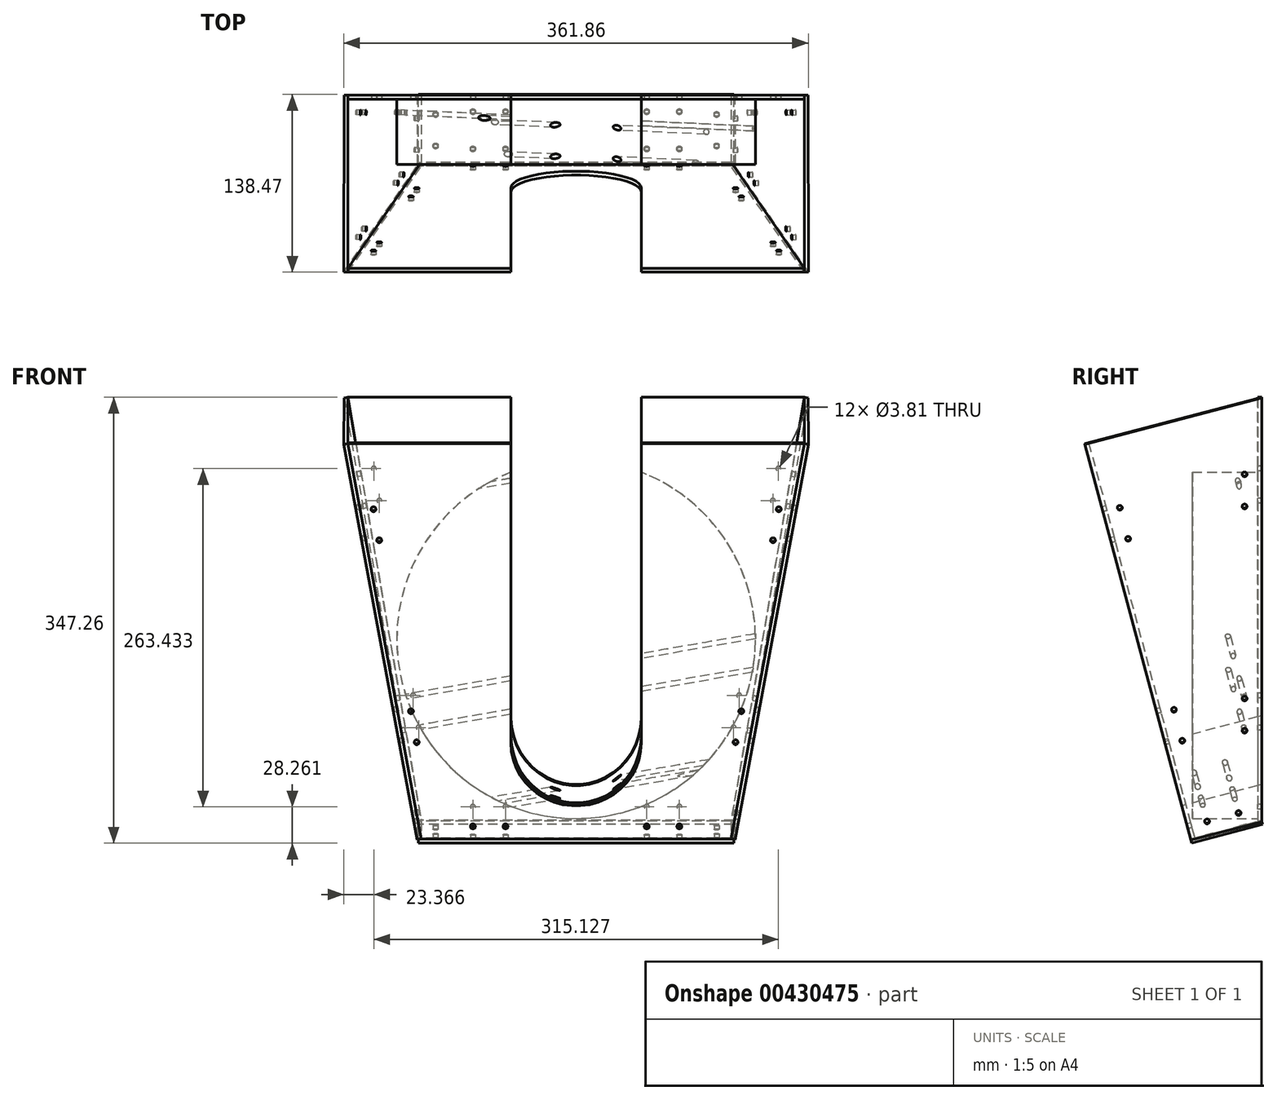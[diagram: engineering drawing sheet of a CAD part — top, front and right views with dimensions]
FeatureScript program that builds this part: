
annotation { "Feature Type Name" : "Feature", "Feature Type Description" : "" }
export const myFeature = defineFeature(function(context is Context, id is Id, definition is map)
    precondition{}
    {
        {
            var Q0;
            Q0=qCreatedBy(makeId("Right.planeOp"),FACE);
            var sketch = newSketch(context, id + "F0", { "sketchPlane" : qUnion([Q0])});
            skLineSegment(sketch, "E0.bottom", {"start": v(-164.52, 79.35) * mm, "end": v(-89.48, 66.12) * mm});
            skLineSegment(sketch, "E0.top", {"start": v(-67.49, 629.66) * mm, "end": v(7.56, 616.43) * mm});
            skLineSegment(sketch, "E0.left", {"start": v(-164.52, 79.35) * mm, "end": v(-67.49, 629.66) * mm});
            skLineSegment(sketch, "E0.right", {"start": v(-89.48, 66.12) * mm, "end": v(7.56, 616.43) * mm});
            skLineSegment(sketch, "E1.bottom", {"start": v(0, 38.1) * mm, "end": v(406.4, 38.1) * mm});
            skLineSegment(sketch, "E1.top", {"start": v(0, 546.1) * mm, "end": v(406.4, 546.1) * mm});
            skLineSegment(sketch, "E1.left", {"start": v(0, 38.1) * mm, "end": v(0, 546.1) * mm});
            skLineSegment(sketch, "E1.right", {"start": v(406.4, 38.1) * mm, "end": v(406.4, 546.1) * mm});
            skLineSegment(sketch, "E2.bottom", {"start": v(42.48, 128.48) * mm, "end": v(86.93, 128.48) * mm});
            skLineSegment(sketch, "E2.top", {"start": v(42.48, 84.03) * mm, "end": v(86.93, 84.03) * mm});
            skLineSegment(sketch, "E2.left", {"start": v(42.48, 128.48) * mm, "end": v(42.48, 84.03) * mm});
            skLineSegment(sketch, "E2.right", {"start": v(86.93, 128.48) * mm, "end": v(86.93, 84.03) * mm});
            skPoint(sketch, "E2.middle", {"position": v(64.7, 106.26) * mm});
            skSolve(sketch);
        }
        {
            var Q0;
            Q0=qCreatedBy(makeId("Front.planeOp"),FACE);
            var sketch = newSketch(context, id + "F1", { "sketchPlane" : qUnion([Q0])});
            skLineSegment(sketch, "E3.bottom", {"start": v(177.8, 596.9) * mm, "end": v(-177.8, 596.9) * mm});
            skLineSegment(sketch, "E3.top", {"start": v(120.65, 266.7) * mm, "end": v(-120.65, 266.7) * mm});
            skPoint(sketch, "E3.middle", {"position": v(0, 431.8) * mm});
            skLineSegment(sketch, "E4", {"start": v(-177.8, 596.9) * mm, "end": v(-120.65, 266.7) * mm});
            skLineSegment(sketch, "E5", {"start": v(0, 596.9) * mm, "end": v(0, 604.14) * mm, "construction": true});
            skPoint(sketch, "E5.endSnap0", {"position": v(0, 596.9) * mm});
            skLineSegment(sketch, "E6.MirrorCS", {"start": v(177.8, 596.9) * mm, "end": v(120.65, 266.7) * mm});
            skCircle(sketch, "E7", {"center": v(0, 408.44) * mm, "radius": 139.7 * mm, "construction": true});
            skCircle(sketch, "E8", {"center": v(0, 330.2) * mm, "radius": 17.46 * mm, "construction": true});
            skPoint(sketch, "E3.left.end.orphan", {"position": v(177.8, 266.7) * mm});
            skPoint(sketch, "E9.orphan", {"position": v(-177.8, 266.7) * mm});
            skSolve(sketch);
        }
        {
            var Q0;
            Q0 = qSketchRegion(id + "F1", true);
            extrude(context, id + "F2", {"entities" : qUnion([Q0]), "oppositeDirection" : true, "depth" : 3.17 * mm});
        }
        {
            var Q0;
            Q0=makeQuery(id+"F1.imprint","IMPRINT",FACE,{"disambiguationData":[TD([[makeQuery(id+"F1.imprint","IMPRINT",EDGE,{"derivedFrom":sQuery(id+"F1.wireOp",EDGE,"E3.bottom")}),1.0]])]});
            var sketch = newSketch(context, id + "F3", { "sketchPlane" : qUnion([Q0])});
            skCircle(sketch, "E10.0", {"center": v(0, 408.44) * mm, "radius": 139.7 * mm});
            skSolve(sketch);
        }
        {
            var Q0;
            Q0 = qSketchRegion(id + "F3", true);
            extrude(context, id + "F4", {"entities" : qUnion([Q0]), "depth" : 50.8 * mm});
        }
        {
            var Q0;
            Q0=makeQuery(id+"F4.opExtrude","CAP_FACE",FACE,{"disambiguationData":[OSD([sQuery(id+"F3.wireOp",EDGE,"E10.0")])],"isStart":false});
            var Q1;
            Q1=sQuery(id+"F1.wireOp",EDGE,"E3.top");
            cPlane(context, id + "F5", {"entities" : qUnion([Q0, Q1]), "cplaneType" : CPlaneType.LINE_ANGLE, "offset" : 25.4 * mm, "angle" : 345 * degree, "width" : 152.4 * mm, "height" : 152.4 * mm});
        }
        {
            var Q0;
            Q0=qCreatedBy(id+"F5.planeOp",FACE);
            cPlane(context, id + "F6", {"entities" : qUnion([Q0]), "cplaneType" : CPlaneType.OFFSET, "offset" : 53.97 * mm, "oppositeDirection" : true, "width" : 152.4 * mm, "height" : 152.4 * mm});
        }
        {
            var Q0;
            Q0=qCreatedBy(id+"F6.planeOp",FACE);
            var sketch = newSketch(context, id + "F7", { "sketchPlane" : qUnion([Q0])});
            skLineSegment(sketch, "E11.0", {"start": v(177.8, 576.56) * mm, "end": v(120.65, 257.61) * mm});
            skLineSegment(sketch, "E11.1", {"start": v(-177.8, 576.56) * mm, "end": v(177.8, 576.56) * mm});
            skLineSegment(sketch, "E11.2", {"start": v(-177.8, 576.56) * mm, "end": v(-120.65, 257.61) * mm});
            skLineSegment(sketch, "E11.3", {"start": v(-120.65, 257.61) * mm, "end": v(120.65, 257.61) * mm});
            skSolve(sketch);
        }
        {
            var Q0;
            Q0=makeQuery(id+"F7.imprint","IMPRINT",FACE,{"disambiguationData":[TD([[makeQuery(id+"F7.imprint","IMPRINT",EDGE,{"derivedFrom":sQuery(id+"F7.wireOp",EDGE,"E11.0")}),-1.0]])]});
            extrude(context, id + "F8", {"entities" : qUnion([Q0]), "depth" : 3.17 * mm});
        }
        {
            var Q0;
            Q0=makeQuery(id+"F8.opExtrude","SWEPT_FACE",FACE,{"disambiguationData":[OSD([sQuery(id+"F7.wireOp",EDGE,"E11.0")])]});
            var sketch = newSketch(context, id + "F9", { "sketchPlane" : qUnion([Q0])});
            skLineSegment(sketch, "E12.0", {"start": v(0.18, 618.48) * mm, "end": v(0.18, 283.37) * mm});
            skLineSegment(sketch, "E13.0", {"start": v(138.18, 582.92) * mm, "end": v(55.54, 269.6) * mm});
            skLineSegment(sketch, "E14", {"start": v(0.18, 283.37) * mm, "end": v(52.47, 270.41) * mm});
            skLineSegment(sketch, "E15", {"start": v(0.18, 618.48) * mm, "end": v(138.18, 582.92) * mm});
            skSolve(sketch);
        }
        {
            var Q0;
            {var subQ0=sQuery(id+"F9.wireOp",EDGE,"E12.0");Q0=makeQuery(id+"F9.imprint","IMPRINT",FACE,{"disambiguationData":[TD([[makeQuery(id+"F9.imprint","IMPRINT",EDGE,{"derivedFrom":subQ0}),1.0]])]});}
            var Q1;
            {var subQ0=sQuery(id+"F9.wireOp",EDGE,"E13.0");Q1=makeQuery(id+"F9.imprint","IMPRINT",FACE,{"disambiguationData":[TD([[makeQuery(id+"F9.imprint","IMPRINT",EDGE,{"derivedFrom":subQ0}),-1.0]])]});}
            extrude(context, id + "F10", {"entities" : qUnion([Q0, Q1]), "depth" : 3.17 * mm});
        }
        {
            var Q0;
            Q0=makeQuery(id+"F10.opExtrude","SWEPT_BODY",BODY,{"disambiguationData":[OSD([sQuery(id+"F7.wireOp",EDGE,"E11.0"),sQuery(id+"F9.wireOp",EDGE,"E12.0"),sQuery(id+"F9.wireOp",EDGE,"E14"),sQuery(id+"F9.wireOp",EDGE,"E15")])]});
            var Q1;
            Q1=qCreatedBy(makeId("Right.planeOp"),FACE);
            mirror(context, id + "F11", {"entities" : qUnion([Q0]), "mirrorPlane" : qUnion([Q1])});
        }
        {
            var Q0;
            Q0=makeQuery(id+"F8.opExtrude","SWEPT_FACE",FACE,{"disambiguationData":[OSD([sQuery(id+"F7.wireOp",EDGE,"E11.3")])]});
            var sketch = newSketch(context, id + "F12", { "sketchPlane" : qUnion([Q0])});
            skLineSegment(sketch, "E16.bottom", {"start": v(122.9, -15.05) * mm, "end": v(-122.9, -15.05) * mm});
            skLineSegment(sketch, "E16.top", {"start": v(122.9, -72.1) * mm, "end": v(-122.9, -72.1) * mm});
            skLineSegment(sketch, "E16.left", {"start": v(122.9, -15.05) * mm, "end": v(122.9, -72.1) * mm});
            skLineSegment(sketch, "E16.right", {"start": v(-122.9, -15.05) * mm, "end": v(-122.9, -72.1) * mm});
            skPoint(sketch, "E16.middle", {"position": v(0, -43.57) * mm});
            skSolve(sketch);
        }
        {
            var Q0;
            Q0 = qSketchRegion(id + "F12", true);
            extrude(context, id + "F13", {"entities" : qUnion([Q0]), "depth" : 3.17 * mm});
        }
        {
            var Q0;
            Q0=makeQuery(id+"F8.opExtrude","CAP_FACE",FACE,{"disambiguationData":[OSD([sQuery(id+"F7.wireOp",EDGE,"E11.0"),sQuery(id+"F7.wireOp",EDGE,"E11.1"),sQuery(id+"F7.wireOp",EDGE,"E11.2"),sQuery(id+"F7.wireOp",EDGE,"E11.3")])],"isStart":true});
            var sketch = newSketch(context, id + "F14", { "sketchPlane" : qUnion([Q0])});
            skLineSegment(sketch, "E17", {"start": v(0, 439.09) * mm, "end": v(0, 333.36) * mm, "construction": true});
            skLineSegment(sketch, "E18.bottom", {"start": v(-170.23, 534.32) * mm, "end": v(-149.92, 537.96) * mm, "construction": true});
            skLineSegment(sketch, "E18.top", {"start": v(-161.27, 484.32) * mm, "end": v(-140.96, 487.96) * mm, "construction": true});
            skLineSegment(sketch, "E18.left", {"start": v(-170.23, 534.32) * mm, "end": v(-161.27, 484.32) * mm, "construction": true});
            skLineSegment(sketch, "E18.right", {"start": v(-149.92, 537.96) * mm, "end": v(-140.96, 487.96) * mm, "construction": true});
            skLineSegment(sketch, "E19.bottom", {"start": v(-93.12, 278.25) * mm, "end": v(-42.32, 278.25) * mm, "construction": true});
            skLineSegment(sketch, "E19.top", {"start": v(-93.12, 257.61) * mm, "end": v(-42.32, 257.61) * mm});
            skLineSegment(sketch, "E19.left", {"start": v(-93.12, 278.25) * mm, "end": v(-93.12, 257.61) * mm, "construction": true});
            skLineSegment(sketch, "E19.right", {"start": v(-42.32, 278.25) * mm, "end": v(-42.32, 257.61) * mm, "construction": true});
            skLineSegment(sketch, "E20", {"start": v(-160.07, 536.14) * mm, "end": v(-151.11, 486.14) * mm, "construction": true});
            skLineSegment(sketch, "E21", {"start": v(-93.12, 267.93) * mm, "end": v(-42.32, 267.93) * mm, "construction": true});
            skLineSegment(sketch, "E22", {"start": v(-145.44, 512.96) * mm, "end": v(-165.75, 509.32) * mm, "construction": true});
            skLineSegment(sketch, "E23", {"start": v(-67.72, 278.25) * mm, "end": v(-67.72, 257.61) * mm, "construction": true});
            skCircle(sketch, "E24", {"center": v(-157.83, 523.64) * mm, "radius": 1.9 * mm});
            skCircle(sketch, "E25.MirrorC", {"center": v(-153.35, 498.64) * mm, "radius": 1.9 * mm});
            skLineSegment(sketch, "E26.bottom", {"start": v(-141.04, 371.42) * mm, "end": v(-120.73, 375.06) * mm, "construction": true});
            skLineSegment(sketch, "E26.top", {"start": v(-132.08, 321.41) * mm, "end": v(-111.77, 325.05) * mm, "construction": true});
            skLineSegment(sketch, "E26.left", {"start": v(-141.04, 371.42) * mm, "end": v(-132.08, 321.41) * mm, "construction": true});
            skLineSegment(sketch, "E26.right", {"start": v(-120.73, 375.06) * mm, "end": v(-111.77, 325.05) * mm, "construction": true});
            skLineSegment(sketch, "E27", {"start": v(-130.88, 373.24) * mm, "end": v(-121.92, 323.23) * mm, "construction": true});
            skLineSegment(sketch, "E28", {"start": v(-116.25, 350.05) * mm, "end": v(-136.56, 346.41) * mm, "construction": true});
            skCircle(sketch, "E29", {"center": v(-128.64, 360.73) * mm, "radius": 1.9 * mm});
            skCircle(sketch, "E30.MirrorC", {"center": v(-124.16, 335.73) * mm, "radius": 1.9 * mm});
            skCircle(sketch, "E31", {"center": v(-80.42, 267.93) * mm, "radius": 1.9 * mm});
            skCircle(sketch, "E32.MirrorC", {"center": v(-55.02, 267.93) * mm, "radius": 1.9 * mm});
            skLineSegment(sketch, "E33.MirrorCS", {"start": v(132.08, 321.41) * mm, "end": v(111.77, 325.05) * mm, "construction": true});
            skCircle(sketch, "E34.MirrorC", {"center": v(128.64, 360.73) * mm, "radius": 1.9 * mm});
            skCircle(sketch, "E35.MirrorC", {"center": v(157.83, 523.64) * mm, "radius": 1.9 * mm});
            skLineSegment(sketch, "E36.MirrorCS", {"start": v(42.32, 278.25) * mm, "end": v(42.32, 257.61) * mm, "construction": true});
            skLineSegment(sketch, "E37.MirrorCS", {"start": v(93.12, 278.25) * mm, "end": v(93.12, 257.61) * mm, "construction": true});
            skLineSegment(sketch, "E38.MirrorCS", {"start": v(161.27, 484.32) * mm, "end": v(140.96, 487.96) * mm, "construction": true});
            skCircle(sketch, "E39.MirrorC", {"center": v(55.02, 267.93) * mm, "radius": 1.9 * mm});
            skLineSegment(sketch, "E40.MirrorCS", {"start": v(145.44, 512.96) * mm, "end": v(165.75, 509.32) * mm, "construction": true});
            skLineSegment(sketch, "E41.MirrorCS", {"start": v(170.23, 534.32) * mm, "end": v(149.92, 537.96) * mm, "construction": true});
            skLineSegment(sketch, "E42.MirrorCS", {"start": v(130.88, 373.24) * mm, "end": v(121.92, 323.23) * mm, "construction": true});
            skCircle(sketch, "E43.MirrorC", {"center": v(124.16, 335.73) * mm, "radius": 1.9 * mm});
            skLineSegment(sketch, "E44.MirrorCS", {"start": v(160.07, 536.14) * mm, "end": v(151.11, 486.14) * mm, "construction": true});
            skLineSegment(sketch, "E45.MirrorCS", {"start": v(141.04, 371.42) * mm, "end": v(120.73, 375.06) * mm, "construction": true});
            skCircle(sketch, "E46.MirrorC", {"center": v(153.35, 498.64) * mm, "radius": 1.9 * mm});
            skCircle(sketch, "E47.MirrorC", {"center": v(80.42, 267.93) * mm, "radius": 1.9 * mm});
            skLineSegment(sketch, "E48.MirrorCS", {"start": v(141.04, 371.42) * mm, "end": v(132.08, 321.41) * mm, "construction": true});
            skLineSegment(sketch, "E49.MirrorCS", {"start": v(93.12, 257.61) * mm, "end": v(42.32, 257.61) * mm});
            skLineSegment(sketch, "E50.MirrorCS", {"start": v(116.25, 350.05) * mm, "end": v(136.56, 346.41) * mm, "construction": true});
            skLineSegment(sketch, "E51.MirrorCS", {"start": v(170.23, 534.32) * mm, "end": v(161.27, 484.32) * mm, "construction": true});
            skLineSegment(sketch, "E52.MirrorCS", {"start": v(149.92, 537.96) * mm, "end": v(140.96, 487.96) * mm, "construction": true});
            skLineSegment(sketch, "E53.MirrorCS", {"start": v(120.73, 375.06) * mm, "end": v(111.77, 325.05) * mm, "construction": true});
            skLineSegment(sketch, "E54.MirrorCS", {"start": v(93.12, 267.93) * mm, "end": v(42.32, 267.93) * mm, "construction": true});
            skLineSegment(sketch, "E55.MirrorCS", {"start": v(67.72, 278.25) * mm, "end": v(67.72, 257.61) * mm, "construction": true});
            skLineSegment(sketch, "E56.MirrorCS", {"start": v(93.12, 278.25) * mm, "end": v(42.32, 278.25) * mm, "construction": true});
            skSolve(sketch);
        }
        {
            var Q0;
            Q0 = qSketchRegion(id + "F14", true);
            var Q1;
            Q1=makeQuery(id+"F8.opExtrude","CAP_FACE",FACE,{"disambiguationData":[OSD([sQuery(id+"F7.wireOp",EDGE,"E11.0"),sQuery(id+"F7.wireOp",EDGE,"E11.1"),sQuery(id+"F7.wireOp",EDGE,"E11.2"),sQuery(id+"F7.wireOp",EDGE,"E11.3")])],"isStart":false});
            extrude(context, id + "F15", {"entities" : qUnion([Q0]), "operationType" : NewBodyOperationType.REMOVE, "endBound" : BoundingType.UP_TO_SURFACE, "oppositeDirection" : true, "depth" : 25.4 * mm, "endBoundEntityFace" : qUnion([Q1]), "offsetDistance" : 25.4 * mm});
        }
        {
            var Q0;
            Q0=makeQuery(id+"F10.opExtrude","CAP_FACE",FACE,{"disambiguationData":[OSD([sQuery(id+"F7.wireOp",EDGE,"E11.0"),sQuery(id+"F7.wireOp",EDGE,"E11.3"),sQuery(id+"F9.wireOp",EDGE,"E12.0"),sQuery(id+"F9.wireOp",EDGE,"E13.0"),sQuery(id+"F9.wireOp",EDGE,"E14"),sQuery(id+"F9.wireOp",EDGE,"E15")])],"isStart":false});
            var sketch = newSketch(context, id + "F16", { "sketchPlane" : qUnion([Q0])});
            skLineSegment(sketch, "E57.0", {"start": v(127.23, 541.42) * mm, "end": v(114.28, 492.3) * mm, "construction": true});
            skLineSegment(sketch, "E58.0", {"start": v(85.03, 381.4) * mm, "end": v(72.07, 332.28) * mm, "construction": true});
            skLineSegment(sketch, "E59.bottom", {"start": v(62, 387.47) * mm, "end": v(85.03, 381.4) * mm, "construction": true});
            skLineSegment(sketch, "E59.top", {"start": v(49.05, 338.35) * mm, "end": v(72.07, 332.28) * mm, "construction": true});
            skLineSegment(sketch, "E59.left", {"start": v(62, 387.47) * mm, "end": v(49.05, 338.35) * mm, "construction": true});
            skLineSegment(sketch, "E60", {"start": v(81.96, 382.2) * mm, "end": v(69, 333.09) * mm, "construction": true});
            skPoint(sketch, "E61", {"position": v(71.98, 384.84) * mm});
            skLineSegment(sketch, "E62", {"start": v(71.98, 384.84) * mm, "end": v(59.02, 335.72) * mm, "construction": true});
            skLineSegment(sketch, "E63", {"start": v(55.52, 362.9) * mm, "end": v(75.48, 357.65) * mm, "construction": true});
            skCircle(sketch, "E64", {"center": v(62.26, 348) * mm, "radius": 1.9 * mm});
            skCircle(sketch, "E65.MirrorC", {"center": v(68.74, 372.56) * mm, "radius": 1.9 * mm});
            skLineSegment(sketch, "E66.bottom", {"start": v(104.2, 547.5) * mm, "end": v(127.23, 541.42) * mm, "construction": true});
            skLineSegment(sketch, "E66.top", {"start": v(91.25, 498.37) * mm, "end": v(114.28, 492.3) * mm, "construction": true});
            skLineSegment(sketch, "E66.left", {"start": v(104.2, 547.5) * mm, "end": v(91.25, 498.37) * mm, "construction": true});
            skLineSegment(sketch, "E67", {"start": v(124.16, 542.23) * mm, "end": v(111.2, 493.11) * mm, "construction": true});
            skPoint(sketch, "E68", {"position": v(114.18, 544.86) * mm});
            skLineSegment(sketch, "E69", {"start": v(114.18, 544.86) * mm, "end": v(101.23, 495.74) * mm, "construction": true});
            skLineSegment(sketch, "E70", {"start": v(97.73, 522.93) * mm, "end": v(117.68, 517.67) * mm, "construction": true});
            skCircle(sketch, "E71", {"center": v(104.47, 508.02) * mm, "radius": 1.9 * mm});
            skCircle(sketch, "E72.MirrorC", {"center": v(110.95, 532.58) * mm, "radius": 1.9 * mm});
            skLineSegment(sketch, "E73.bottom", {"start": v(3.35, 570.93) * mm, "end": v(24, 570.93) * mm, "construction": true});
            skLineSegment(sketch, "E73.top", {"start": v(3.35, 520.13) * mm, "end": v(24, 520.13) * mm, "construction": true});
            skLineSegment(sketch, "E73.left", {"start": v(3.35, 570.93) * mm, "end": v(3.35, 520.13) * mm, "construction": true});
            skLineSegment(sketch, "E73.right", {"start": v(24, 570.93) * mm, "end": v(24, 520.13) * mm, "construction": true});
            skLineSegment(sketch, "E74.bottom", {"start": v(3.35, 570.93) * mm, "end": v(0.18, 570.93) * mm, "construction": true});
            skLineSegment(sketch, "E74.top", {"start": v(3.35, 520.13) * mm, "end": v(0.18, 520.13) * mm, "construction": true});
            skLineSegment(sketch, "E74.right", {"start": v(0.18, 570.93) * mm, "end": v(0.18, 520.13) * mm, "construction": true});
            skLineSegment(sketch, "E75", {"start": v(13.67, 570.93) * mm, "end": v(13.67, 520.13) * mm, "construction": true});
            skLineSegment(sketch, "E76", {"start": v(24, 545.53) * mm, "end": v(3.35, 545.53) * mm, "construction": true});
            skCircle(sketch, "E77", {"center": v(13.67, 558.23) * mm, "radius": 1.9 * mm});
            skCircle(sketch, "E78.MirrorC", {"center": v(13.67, 532.83) * mm, "radius": 1.9 * mm});
            skLineSegment(sketch, "E79.bottom", {"start": v(3.35, 393.68) * mm, "end": v(24, 393.68) * mm, "construction": true});
            skLineSegment(sketch, "E79.top", {"start": v(3.35, 342.88) * mm, "end": v(24, 342.88) * mm, "construction": true});
            skLineSegment(sketch, "E79.left", {"start": v(3.35, 393.68) * mm, "end": v(3.35, 342.88) * mm, "construction": true});
            skLineSegment(sketch, "E79.right", {"start": v(24, 393.68) * mm, "end": v(24, 342.88) * mm, "construction": true});
            skLineSegment(sketch, "E80.bottom", {"start": v(3.35, 393.68) * mm, "end": v(0.18, 393.68) * mm, "construction": true});
            skLineSegment(sketch, "E80.top", {"start": v(3.35, 342.88) * mm, "end": v(0.18, 342.88) * mm, "construction": true});
            skLineSegment(sketch, "E80.right", {"start": v(0.18, 393.68) * mm, "end": v(0.18, 342.88) * mm, "construction": true});
            skLineSegment(sketch, "E81", {"start": v(13.67, 393.68) * mm, "end": v(13.67, 342.88) * mm, "construction": true});
            skLineSegment(sketch, "E82", {"start": v(24, 368.28) * mm, "end": v(3.35, 368.28) * mm, "construction": true});
            skCircle(sketch, "E83", {"center": v(13.67, 380.98) * mm, "radius": 1.9 * mm});
            skCircle(sketch, "E84.MirrorC", {"center": v(13.67, 355.58) * mm, "radius": 1.9 * mm});
            skLineSegment(sketch, "E85.bottom", {"start": v(8.73, 303.76) * mm, "end": v(57.85, 290.8) * mm, "construction": true});
            skLineSegment(sketch, "E85.top", {"start": v(3.46, 283.8) * mm, "end": v(52.58, 270.85) * mm, "construction": true});
            skLineSegment(sketch, "E85.left", {"start": v(8.73, 303.76) * mm, "end": v(3.46, 283.8) * mm, "construction": true});
            skLineSegment(sketch, "E85.right", {"start": v(57.85, 290.8) * mm, "end": v(52.58, 270.85) * mm, "construction": true});
            skLineSegment(sketch, "E86.top", {"start": v(2.65, 280.73) * mm, "end": v(51.77, 267.78) * mm, "construction": true});
            skLineSegment(sketch, "E86.left", {"start": v(3.46, 283.8) * mm, "end": v(2.65, 280.73) * mm, "construction": true});
            skLineSegment(sketch, "E86.right", {"start": v(52.58, 270.85) * mm, "end": v(51.77, 267.78) * mm, "construction": true});
            skLineSegment(sketch, "E87", {"start": v(6.1, 293.78) * mm, "end": v(55.22, 280.82) * mm, "construction": true});
            skLineSegment(sketch, "E88", {"start": v(33.29, 297.28) * mm, "end": v(28.02, 277.32) * mm, "construction": true});
            skCircle(sketch, "E89", {"center": v(18.38, 290.54) * mm, "radius": 1.9 * mm});
            skCircle(sketch, "E90.MirrorC", {"center": v(42.94, 284.06) * mm, "radius": 1.9 * mm});
            skSolve(sketch);
        }
        {
            var Q0;
            Q0 = qSketchRegion(id + "F16", true);
            extrude(context, id + "F17", {"entities" : qUnion([Q0]), "operationType" : NewBodyOperationType.REMOVE, "endBound" : BoundingType.THROUGH_ALL, "oppositeDirection" : true, "depth" : 25.4 * mm, "offsetDistance" : 25.4 * mm});
        }
        {
            var Q0;
            Q0=makeQuery(id+"F11.opPattern","COPY",BODY,{"derivedFrom":makeQuery(id+"F10.opExtrude","SWEPT_BODY",BODY,{"disambiguationData":[OSD([sQuery(id+"F7.wireOp",EDGE,"E11.0"),sQuery(id+"F7.wireOp",EDGE,"E11.3"),sQuery(id+"F9.wireOp",EDGE,"E12.0"),sQuery(id+"F9.wireOp",EDGE,"E13.0"),sQuery(id+"F9.wireOp",EDGE,"E14"),sQuery(id+"F9.wireOp",EDGE,"E15")])]}),"instanceName":"1"});
            deleteBodies(context, id + "F18", {"entities" : qUnion([Q0])});
        }
        {
            var Q0;
            Q0=makeQuery(id+"F10.opExtrude","SWEPT_BODY",BODY,{"disambiguationData":[OSD([sQuery(id+"F7.wireOp",EDGE,"E11.0"),sQuery(id+"F7.wireOp",EDGE,"E11.3"),sQuery(id+"F9.wireOp",EDGE,"E12.0"),sQuery(id+"F9.wireOp",EDGE,"E13.0"),sQuery(id+"F9.wireOp",EDGE,"E14"),sQuery(id+"F9.wireOp",EDGE,"E15")])]});
            var Q1;
            Q1=qCreatedBy(makeId("Right.planeOp"),FACE);
            mirror(context, id + "F19", {"entities" : qUnion([Q0]), "mirrorPlane" : qUnion([Q1])});
        }
        {
            var Q0;
            Q0=makeQuery(id+"F1.imprint","IMPRINT",FACE,{"disambiguationData":[TD([[makeQuery(id+"F1.imprint","IMPRINT",EDGE,{"derivedFrom":sQuery(id+"F1.wireOp",EDGE,"E3.bottom")}),1.0]])]});
            var sketch = newSketch(context, id + "F20", { "sketchPlane" : qUnion([Q0])});
            skLineSegment(sketch, "E91.0", {"start": v(-172.82, 549.5) * mm, "end": v(-164.15, 499.45) * mm, "construction": true});
            skLineSegment(sketch, "E92.bottom", {"start": v(-169.9, 552.1) * mm, "end": v(-173.03, 551.57) * mm, "construction": true});
            skLineSegment(sketch, "E92.top", {"start": v(-161.23, 502.05) * mm, "end": v(-164.36, 501.51) * mm, "construction": true});
            skLineSegment(sketch, "E92.left", {"start": v(-169.9, 552.1) * mm, "end": v(-161.23, 502.05) * mm, "construction": true});
            skLineSegment(sketch, "E92.right", {"start": v(-173.03, 551.57) * mm, "end": v(-164.36, 501.51) * mm, "construction": true});
            skLineSegment(sketch, "E93.bottom", {"start": v(-149.56, 555.63) * mm, "end": v(-169.9, 552.1) * mm, "construction": true});
            skLineSegment(sketch, "E93.top", {"start": v(-140.9, 505.57) * mm, "end": v(-161.23, 502.05) * mm, "construction": true});
            skLineSegment(sketch, "E93.left", {"start": v(-149.56, 555.63) * mm, "end": v(-140.9, 505.57) * mm, "construction": true});
            skLineSegment(sketch, "E94", {"start": v(-159.73, 553.87) * mm, "end": v(-151.07, 503.81) * mm, "construction": true});
            skLineSegment(sketch, "E95", {"start": v(-145.23, 530.6) * mm, "end": v(-165.57, 527.08) * mm, "construction": true});
            skCircle(sketch, "E96", {"center": v(-157.56, 541.35) * mm, "radius": 1.9 * mm});
            skCircle(sketch, "E97.MirrorC", {"center": v(-153.23, 516.33) * mm, "radius": 1.9 * mm});
            skLineSegment(sketch, "E98", {"start": v(0, 542.09) * mm, "end": v(0, 433.89) * mm, "construction": true});
            skLineSegment(sketch, "E99.0", {"start": v(-137.98, 349.1) * mm, "end": v(-129.32, 299.04) * mm, "construction": true});
            skLineSegment(sketch, "E100.bottom", {"start": v(-139.32, 375.42) * mm, "end": v(-142.45, 374.88) * mm, "construction": true});
            skLineSegment(sketch, "E100.top", {"start": v(-130.65, 325.37) * mm, "end": v(-133.78, 324.83) * mm, "construction": true});
            skLineSegment(sketch, "E100.left", {"start": v(-139.32, 375.42) * mm, "end": v(-130.65, 325.37) * mm, "construction": true});
            skLineSegment(sketch, "E100.right", {"start": v(-142.45, 374.88) * mm, "end": v(-133.78, 324.83) * mm, "construction": true});
            skLineSegment(sketch, "E101.bottom", {"start": v(-118.98, 378.94) * mm, "end": v(-139.32, 375.42) * mm, "construction": true});
            skLineSegment(sketch, "E101.top", {"start": v(-110.32, 328.89) * mm, "end": v(-130.65, 325.37) * mm, "construction": true});
            skLineSegment(sketch, "E101.left", {"start": v(-118.98, 378.94) * mm, "end": v(-110.32, 328.89) * mm, "construction": true});
            skLineSegment(sketch, "E102", {"start": v(-129.15, 377.18) * mm, "end": v(-120.49, 327.13) * mm, "construction": true});
            skLineSegment(sketch, "E103", {"start": v(-114.65, 353.92) * mm, "end": v(-134.99, 350.4) * mm, "construction": true});
            skCircle(sketch, "E104", {"center": v(-126.98, 364.67) * mm, "radius": 1.9 * mm});
            skCircle(sketch, "E105.MirrorC", {"center": v(-122.65, 339.64) * mm, "radius": 1.9 * mm});
            skLineSegment(sketch, "E106.bottom", {"start": v(-42.32, 288.24) * mm, "end": v(-93.12, 288.24) * mm, "construction": true});
            skLineSegment(sketch, "E106.top", {"start": v(-42.32, 267.6) * mm, "end": v(-93.12, 267.6) * mm, "construction": true});
            skLineSegment(sketch, "E106.left", {"start": v(-42.32, 288.24) * mm, "end": v(-42.32, 267.6) * mm, "construction": true});
            skLineSegment(sketch, "E106.right", {"start": v(-93.12, 288.24) * mm, "end": v(-93.12, 267.6) * mm, "construction": true});
            skLineSegment(sketch, "E107.top", {"start": v(-42.32, 264.43) * mm, "end": v(-93.12, 264.43) * mm, "construction": true});
            skLineSegment(sketch, "E107.left", {"start": v(-42.32, 267.6) * mm, "end": v(-42.32, 264.43) * mm, "construction": true});
            skLineSegment(sketch, "E107.right", {"start": v(-93.12, 267.6) * mm, "end": v(-93.12, 264.43) * mm, "construction": true});
            skLineSegment(sketch, "E108", {"start": v(-42.32, 277.92) * mm, "end": v(-93.12, 277.92) * mm, "construction": true});
            skLineSegment(sketch, "E109", {"start": v(-67.72, 288.24) * mm, "end": v(-67.72, 267.6) * mm, "construction": true});
            skCircle(sketch, "E110", {"center": v(-55.02, 277.92) * mm, "radius": 1.9 * mm});
            skCircle(sketch, "E111.MirrorC", {"center": v(-80.42, 277.92) * mm, "radius": 1.9 * mm});
            skLineSegment(sketch, "E112.MirrorCS", {"start": v(161.23, 502.05) * mm, "end": v(164.36, 501.51) * mm, "construction": true});
            skLineSegment(sketch, "E113.MirrorCS", {"start": v(169.9, 552.1) * mm, "end": v(173.03, 551.57) * mm, "construction": true});
            skLineSegment(sketch, "E114.MirrorCS", {"start": v(139.32, 375.42) * mm, "end": v(142.45, 374.88) * mm, "construction": true});
            skLineSegment(sketch, "E115.MirrorCS", {"start": v(130.65, 325.37) * mm, "end": v(133.78, 324.83) * mm, "construction": true});
            skLineSegment(sketch, "E116.MirrorCS", {"start": v(42.32, 267.6) * mm, "end": v(42.32, 264.43) * mm, "construction": true});
            skLineSegment(sketch, "E117.MirrorCS", {"start": v(93.12, 267.6) * mm, "end": v(93.12, 264.43) * mm, "construction": true});
            skLineSegment(sketch, "E118.MirrorCS", {"start": v(139.32, 375.42) * mm, "end": v(130.65, 325.37) * mm, "construction": true});
            skCircle(sketch, "E119.MirrorC", {"center": v(126.98, 364.67) * mm, "radius": 1.9 * mm});
            skLineSegment(sketch, "E120.MirrorCS", {"start": v(169.9, 552.1) * mm, "end": v(161.23, 502.05) * mm, "construction": true});
            skLineSegment(sketch, "E121.MirrorCS", {"start": v(172.82, 549.5) * mm, "end": v(164.15, 499.45) * mm, "construction": true});
            skLineSegment(sketch, "E122.MirrorCS", {"start": v(142.45, 374.88) * mm, "end": v(133.78, 324.83) * mm, "construction": true});
            skLineSegment(sketch, "E123.MirrorCS", {"start": v(173.03, 551.57) * mm, "end": v(164.36, 501.51) * mm, "construction": true});
            skLineSegment(sketch, "E124.MirrorCS", {"start": v(42.32, 264.43) * mm, "end": v(93.12, 264.43) * mm, "construction": true});
            skLineSegment(sketch, "E125.MirrorCS", {"start": v(129.15, 377.18) * mm, "end": v(120.49, 327.13) * mm, "construction": true});
            skLineSegment(sketch, "E126.MirrorCS", {"start": v(42.32, 288.24) * mm, "end": v(42.32, 267.6) * mm, "construction": true});
            skCircle(sketch, "E127.MirrorC", {"center": v(153.23, 516.33) * mm, "radius": 1.9 * mm});
            skLineSegment(sketch, "E128.MirrorCS", {"start": v(140.9, 505.57) * mm, "end": v(161.23, 502.05) * mm, "construction": true});
            skLineSegment(sketch, "E129.MirrorCS", {"start": v(149.56, 555.63) * mm, "end": v(169.9, 552.1) * mm, "construction": true});
            skLineSegment(sketch, "E130.MirrorCS", {"start": v(145.23, 530.6) * mm, "end": v(165.57, 527.08) * mm, "construction": true});
            skLineSegment(sketch, "E131.MirrorCS", {"start": v(118.98, 378.94) * mm, "end": v(110.32, 328.89) * mm, "construction": true});
            skLineSegment(sketch, "E132.MirrorCS", {"start": v(118.98, 378.94) * mm, "end": v(139.32, 375.42) * mm, "construction": true});
            skCircle(sketch, "E133.MirrorC", {"center": v(157.56, 541.35) * mm, "radius": 1.9 * mm});
            skLineSegment(sketch, "E134.MirrorCS", {"start": v(93.12, 288.24) * mm, "end": v(93.12, 267.6) * mm, "construction": true});
            skLineSegment(sketch, "E135.MirrorCS", {"start": v(159.73, 553.87) * mm, "end": v(151.07, 503.81) * mm, "construction": true});
            skLineSegment(sketch, "E136.MirrorCS", {"start": v(42.32, 267.6) * mm, "end": v(93.12, 267.6) * mm, "construction": true});
            skCircle(sketch, "E137.MirrorC", {"center": v(122.65, 339.64) * mm, "radius": 1.9 * mm});
            skLineSegment(sketch, "E138.MirrorCS", {"start": v(114.65, 353.92) * mm, "end": v(134.99, 350.4) * mm, "construction": true});
            skLineSegment(sketch, "E139.MirrorCS", {"start": v(110.32, 328.89) * mm, "end": v(130.65, 325.37) * mm, "construction": true});
            skLineSegment(sketch, "E140.MirrorCS", {"start": v(137.98, 349.1) * mm, "end": v(129.32, 299.04) * mm, "construction": true});
            skLineSegment(sketch, "E141.MirrorCS", {"start": v(149.56, 555.63) * mm, "end": v(140.9, 505.57) * mm, "construction": true});
            skLineSegment(sketch, "E142.MirrorCS", {"start": v(42.32, 277.92) * mm, "end": v(93.12, 277.92) * mm, "construction": true});
            skCircle(sketch, "E143.MirrorC", {"center": v(55.02, 277.92) * mm, "radius": 1.9 * mm});
            skLineSegment(sketch, "E144.MirrorCS", {"start": v(42.32, 288.24) * mm, "end": v(93.12, 288.24) * mm, "construction": true});
            skLineSegment(sketch, "E145.MirrorCS", {"start": v(67.72, 288.24) * mm, "end": v(67.72, 267.6) * mm, "construction": true});
            skCircle(sketch, "E146.MirrorC", {"center": v(80.42, 277.92) * mm, "radius": 1.9 * mm});
            skSolve(sketch);
        }
        {
            var Q0;
            Q0 = qSketchRegion(id + "F20", true);
            var Q1;
            Q1=sQuery(id+"F20.wireOp",EDGE,"E96");
            var Q2;
            Q2=sQuery(id+"F20.wireOp",EDGE,"E97.MirrorC");
            var Q3;
            Q3=sQuery(id+"F20.wireOp",EDGE,"E127.MirrorC");
            var Q4;
            Q4=sQuery(id+"F20.wireOp",EDGE,"E133.MirrorC");
            var Q5;
            Q5=sQuery(id+"F20.wireOp",EDGE,"E119.MirrorC");
            var Q6;
            Q6=sQuery(id+"F20.wireOp",EDGE,"E137.MirrorC");
            var Q7;
            Q7=sQuery(id+"F20.wireOp",EDGE,"E146.MirrorC");
            var Q8;
            Q8=sQuery(id+"F20.wireOp",EDGE,"E143.MirrorC");
            var Q9;
            Q9=sQuery(id+"F20.wireOp",EDGE,"E110");
            var Q10;
            Q10=sQuery(id+"F20.wireOp",EDGE,"E111.MirrorC");
            var Q11;
            Q11=sQuery(id+"F20.wireOp",EDGE,"E104");
            var Q12;
            Q12=sQuery(id+"F20.wireOp",EDGE,"E105.MirrorC");
            var Q13;
            Q13=makeQuery(id+"F2.opExtrude","CAP_FACE",FACE,{"disambiguationData":[OSD([sQuery(id+"F1.wireOp",EDGE,"E3.bottom"),sQuery(id+"F1.wireOp",EDGE,"E3.top"),sQuery(id+"F1.wireOp",EDGE,"E4"),sQuery(id+"F1.wireOp",EDGE,"E6.MirrorCS")])],"isStart":false});
            extrude(context, id + "F21", {"entities" : qUnion([Q0]), "operationType" : NewBodyOperationType.REMOVE, "surfaceEntities" : qUnion([Q1, Q2, Q3, Q4, Q5, Q6, Q7, Q8, Q9, Q10, Q11, Q12]), "endBound" : BoundingType.UP_TO_SURFACE, "oppositeDirection" : true, "depth" : 25.4 * mm, "endBoundEntityFace" : qUnion([Q13]), "offsetDistance" : 25.4 * mm});
        }
        {
            var Q0;
            Q0=makeQuery(id+"F13.opExtrude","CAP_FACE",FACE,{"disambiguationData":[OSD([sQuery(id+"F12.wireOp",EDGE,"E16.bottom"),sQuery(id+"F12.wireOp",EDGE,"E16.top"),sQuery(id+"F12.wireOp",EDGE,"E16.left"),sQuery(id+"F12.wireOp",EDGE,"E16.right")])],"isStart":false});
            var sketch = newSketch(context, id + "F22", { "sketchPlane" : qUnion([Q0])});
            skLineSegment(sketch, "E147", {"start": v(0, -15.05) * mm, "end": v(0, -38.18) * mm, "construction": true});
            skLineSegment(sketch, "E148.bottom", {"start": v(-93.12, -18.23) * mm, "end": v(-42.32, -18.23) * mm, "construction": true});
            skLineSegment(sketch, "E148.top", {"start": v(-93.12, -38.86) * mm, "end": v(-42.32, -38.86) * mm, "construction": true});
            skLineSegment(sketch, "E148.left", {"start": v(-93.12, -18.23) * mm, "end": v(-93.12, -38.86) * mm, "construction": true});
            skLineSegment(sketch, "E148.right", {"start": v(-42.32, -18.23) * mm, "end": v(-42.32, -38.86) * mm, "construction": true});
            skLineSegment(sketch, "E149.top", {"start": v(-93.12, -15.05) * mm, "end": v(-42.32, -15.05) * mm, "construction": true});
            skLineSegment(sketch, "E149.left", {"start": v(-93.12, -18.23) * mm, "end": v(-93.12, -15.05) * mm, "construction": true});
            skLineSegment(sketch, "E149.right", {"start": v(-42.32, -18.23) * mm, "end": v(-42.32, -15.05) * mm, "construction": true});
            skLineSegment(sketch, "E150", {"start": v(-93.12, -28.55) * mm, "end": v(-42.32, -28.55) * mm, "construction": true});
            skLineSegment(sketch, "E151", {"start": v(-67.72, -38.86) * mm, "end": v(-67.72, -18.23) * mm, "construction": true});
            skCircle(sketch, "E152", {"center": v(-80.42, -28.55) * mm, "radius": 1.9 * mm});
            skCircle(sketch, "E153.MirrorC", {"center": v(-55.02, -28.55) * mm, "radius": 1.9 * mm});
            skLineSegment(sketch, "E154.bottom", {"start": v(-93.12, -48.28) * mm, "end": v(-42.32, -48.28) * mm, "construction": true});
            skLineSegment(sketch, "E154.top", {"start": v(-93.12, -68.92) * mm, "end": v(-42.32, -68.92) * mm, "construction": true});
            skLineSegment(sketch, "E154.left", {"start": v(-93.12, -48.28) * mm, "end": v(-93.12, -68.92) * mm, "construction": true});
            skLineSegment(sketch, "E154.right", {"start": v(-42.32, -48.28) * mm, "end": v(-42.32, -68.92) * mm, "construction": true});
            skLineSegment(sketch, "E155.top", {"start": v(-93.12, -72.1) * mm, "end": v(-42.32, -72.1) * mm, "construction": true});
            skLineSegment(sketch, "E155.left", {"start": v(-93.12, -68.92) * mm, "end": v(-93.12, -72.1) * mm, "construction": true});
            skLineSegment(sketch, "E155.right", {"start": v(-42.32, -68.92) * mm, "end": v(-42.32, -72.1) * mm, "construction": true});
            skLineSegment(sketch, "E156", {"start": v(-67.72, -48.28) * mm, "end": v(-67.72, -68.92) * mm, "construction": true});
            skLineSegment(sketch, "E157", {"start": v(-93.12, -58.6) * mm, "end": v(-42.32, -58.6) * mm, "construction": true});
            skCircle(sketch, "E158", {"center": v(-80.42, -58.6) * mm, "radius": 1.9 * mm});
            skCircle(sketch, "E159.MirrorC", {"center": v(-55.02, -58.6) * mm, "radius": 1.9 * mm});
            skLineSegment(sketch, "E160.bottom", {"start": v(-119.72, -18.23) * mm, "end": v(-99.09, -18.23) * mm, "construction": true});
            skLineSegment(sketch, "E160.top", {"start": v(-119.72, -69.03) * mm, "end": v(-99.09, -69.03) * mm, "construction": true});
            skLineSegment(sketch, "E160.left", {"start": v(-119.72, -18.23) * mm, "end": v(-119.72, -69.03) * mm, "construction": true});
            skLineSegment(sketch, "E160.right", {"start": v(-99.09, -18.23) * mm, "end": v(-99.09, -69.03) * mm, "construction": true});
            skLineSegment(sketch, "E161.bottom", {"start": v(-119.72, -18.23) * mm, "end": v(-122.9, -18.23) * mm, "construction": true});
            skLineSegment(sketch, "E161.top", {"start": v(-119.72, -69.03) * mm, "end": v(-122.9, -69.03) * mm, "construction": true});
            skLineSegment(sketch, "E161.right", {"start": v(-122.9, -18.23) * mm, "end": v(-122.9, -69.03) * mm, "construction": true});
            skLineSegment(sketch, "E162", {"start": v(-99.09, -43.63) * mm, "end": v(-119.72, -43.63) * mm, "construction": true});
            skLineSegment(sketch, "E163", {"start": v(-109.4, -18.23) * mm, "end": v(-109.4, -69.03) * mm, "construction": true});
            skCircle(sketch, "E164", {"center": v(-109.4, -30.93) * mm, "radius": 1.9 * mm});
            skCircle(sketch, "E165.MirrorC", {"center": v(-109.4, -56.33) * mm, "radius": 1.9 * mm});
            skLineSegment(sketch, "E166.MirrorCS", {"start": v(93.12, -18.23) * mm, "end": v(93.12, -15.05) * mm, "construction": true});
            skLineSegment(sketch, "E167.MirrorCS", {"start": v(42.32, -18.23) * mm, "end": v(42.32, -15.05) * mm, "construction": true});
            skLineSegment(sketch, "E168.MirrorCS", {"start": v(119.72, -18.23) * mm, "end": v(122.9, -18.23) * mm, "construction": true});
            skLineSegment(sketch, "E169.MirrorCS", {"start": v(119.72, -69.03) * mm, "end": v(122.9, -69.03) * mm, "construction": true});
            skLineSegment(sketch, "E170.MirrorCS", {"start": v(42.32, -68.92) * mm, "end": v(42.32, -72.1) * mm, "construction": true});
            skLineSegment(sketch, "E171.MirrorCS", {"start": v(93.12, -68.92) * mm, "end": v(93.12, -72.1) * mm, "construction": true});
            skLineSegment(sketch, "E172.MirrorCS", {"start": v(93.12, -18.23) * mm, "end": v(42.32, -18.23) * mm, "construction": true});
            skLineSegment(sketch, "E173.MirrorCS", {"start": v(119.72, -18.23) * mm, "end": v(119.72, -69.03) * mm, "construction": true});
            skLineSegment(sketch, "E174.MirrorCS", {"start": v(93.12, -68.92) * mm, "end": v(42.32, -68.92) * mm, "construction": true});
            skCircle(sketch, "E175.MirrorC", {"center": v(109.4, -30.93) * mm, "radius": 1.9 * mm});
            skLineSegment(sketch, "E176.MirrorCS", {"start": v(93.12, -38.86) * mm, "end": v(42.32, -38.86) * mm, "construction": true});
            skCircle(sketch, "E177.MirrorC", {"center": v(80.42, -58.6) * mm, "radius": 1.9 * mm});
            skLineSegment(sketch, "E178.MirrorCS", {"start": v(42.32, -48.28) * mm, "end": v(42.32, -68.92) * mm, "construction": true});
            skLineSegment(sketch, "E179.MirrorCS", {"start": v(93.12, -48.28) * mm, "end": v(93.12, -68.92) * mm, "construction": true});
            skLineSegment(sketch, "E180.MirrorCS", {"start": v(122.9, -18.23) * mm, "end": v(122.9, -69.03) * mm, "construction": true});
            skLineSegment(sketch, "E181.MirrorCS", {"start": v(119.72, -18.23) * mm, "end": v(99.09, -18.23) * mm, "construction": true});
            skLineSegment(sketch, "E182.MirrorCS", {"start": v(67.72, -48.28) * mm, "end": v(67.72, -68.92) * mm, "construction": true});
            skLineSegment(sketch, "E183.MirrorCS", {"start": v(93.12, -18.23) * mm, "end": v(93.12, -38.86) * mm, "construction": true});
            skLineSegment(sketch, "E184.MirrorCS", {"start": v(93.12, -15.05) * mm, "end": v(42.32, -15.05) * mm, "construction": true});
            skLineSegment(sketch, "E185.MirrorCS", {"start": v(42.32, -18.23) * mm, "end": v(42.32, -38.86) * mm, "construction": true});
            skCircle(sketch, "E186.MirrorC", {"center": v(55.02, -58.6) * mm, "radius": 1.9 * mm});
            skLineSegment(sketch, "E187.MirrorCS", {"start": v(119.72, -69.03) * mm, "end": v(99.09, -69.03) * mm, "construction": true});
            skLineSegment(sketch, "E188.MirrorCS", {"start": v(99.09, -43.63) * mm, "end": v(119.72, -43.63) * mm, "construction": true});
            skLineSegment(sketch, "E189.MirrorCS", {"start": v(93.12, -48.28) * mm, "end": v(42.32, -48.28) * mm, "construction": true});
            skLineSegment(sketch, "E190.MirrorCS", {"start": v(99.09, -18.23) * mm, "end": v(99.09, -69.03) * mm, "construction": true});
            skCircle(sketch, "E191.MirrorC", {"center": v(55.02, -28.55) * mm, "radius": 1.9 * mm});
            skLineSegment(sketch, "E192.MirrorCS", {"start": v(93.12, -58.6) * mm, "end": v(42.32, -58.6) * mm, "construction": true});
            skCircle(sketch, "E193.MirrorC", {"center": v(109.4, -56.33) * mm, "radius": 1.9 * mm});
            skLineSegment(sketch, "E194.MirrorCS", {"start": v(93.12, -72.1) * mm, "end": v(42.32, -72.1) * mm, "construction": true});
            skLineSegment(sketch, "E195.MirrorCS", {"start": v(67.72, -38.86) * mm, "end": v(67.72, -18.23) * mm, "construction": true});
            skCircle(sketch, "E196.MirrorC", {"center": v(80.42, -28.55) * mm, "radius": 1.9 * mm});
            skLineSegment(sketch, "E197.MirrorCS", {"start": v(93.12, -28.55) * mm, "end": v(42.32, -28.55) * mm, "construction": true});
            skLineSegment(sketch, "E198.MirrorCS", {"start": v(109.4, -18.23) * mm, "end": v(109.4, -69.03) * mm, "construction": true});
            skSolve(sketch);
        }
        {
            var Q0;
            Q0 = qSketchRegion(id + "F22", true);
            var Q1;
            Q1=makeQuery(id+"F13.opExtrude","CAP_FACE",FACE,{"disambiguationData":[OSD([sQuery(id+"F12.wireOp",EDGE,"E16.bottom"),sQuery(id+"F12.wireOp",EDGE,"E16.top"),sQuery(id+"F12.wireOp",EDGE,"E16.left"),sQuery(id+"F12.wireOp",EDGE,"E16.right")])],"isStart":true});
            extrude(context, id + "F23", {"entities" : qUnion([Q0]), "operationType" : NewBodyOperationType.REMOVE, "endBound" : BoundingType.UP_TO_SURFACE, "oppositeDirection" : true, "depth" : 25.4 * mm, "endBoundEntityFace" : qUnion([Q1]), "offsetDistance" : 25.4 * mm});
        }
        {
            var Q0;
            Q0=makeQuery(id+"F8.opExtrude","CAP_FACE",FACE,{"disambiguationData":[OSD([sQuery(id+"F7.wireOp",EDGE,"E11.0"),sQuery(id+"F7.wireOp",EDGE,"E11.1"),sQuery(id+"F7.wireOp",EDGE,"E11.2"),sQuery(id+"F7.wireOp",EDGE,"E11.3")])],"isStart":true});
            var sketch = newSketch(context, id + "F24", { "sketchPlane" : qUnion([Q0])});
            skLineSegment(sketch, "E199.top", {"start": v(50.8, 576.56) * mm, "end": v(-50.8, 576.56) * mm});
            skLineSegment(sketch, "E199.left", {"start": v(50.8, 334.36) * mm, "end": v(50.8, 576.56) * mm});
            skLineSegment(sketch, "E199.right", {"start": v(-50.8, 334.36) * mm, "end": v(-50.8, 576.56) * mm});
            skPoint(sketch, "E199.middle", {"position": v(0, 430.51) * mm});
            skLineSegment(sketch, "E200.0", {"start": v(177.8, 576.56) * mm, "end": v(-177.8, 576.56) * mm, "construction": true});
            skArc(sketch, "E201", {"start": v(-50.8, 336.18) * mm, "mid": v(0, 284.46) * mm, "end": v(50.8, 336.18) * mm});
            skPoint(sketch, "E202.orphan", {"position": v(-50.8, 284.46) * mm});
            skPoint(sketch, "E203.orphan", {"position": v(50.8, 284.46) * mm});
            skSolve(sketch);
        }
        {
            var Q0;
            Q0 = qSketchRegion(id + "F24", true);
            var Q1;
            Q1=makeQuery(id+"F8.opExtrude","CAP_FACE",FACE,{"disambiguationData":[OSD([sQuery(id+"F7.wireOp",EDGE,"E11.0"),sQuery(id+"F7.wireOp",EDGE,"E11.1"),sQuery(id+"F7.wireOp",EDGE,"E11.2"),sQuery(id+"F7.wireOp",EDGE,"E11.3")])],"isStart":false});
            extrude(context, id + "F25", {"entities" : qUnion([Q0]), "operationType" : NewBodyOperationType.REMOVE, "endBound" : BoundingType.THROUGH_ALL, "oppositeDirection" : true, "depth" : 25.4 * mm, "endBoundEntityFace" : qUnion([Q1]), "offsetDistance" : 25.4 * mm});
        }
        {
            var Q0;
            Q0=makeQuery(id+"F10.opExtrude","CAP_FACE",FACE,{"disambiguationData":[OSD([sQuery(id+"F7.wireOp",EDGE,"E11.0"),sQuery(id+"F7.wireOp",EDGE,"E11.3"),sQuery(id+"F9.wireOp",EDGE,"E12.0"),sQuery(id+"F9.wireOp",EDGE,"E13.0"),sQuery(id+"F9.wireOp",EDGE,"E14"),sQuery(id+"F9.wireOp",EDGE,"E15")])],"isStart":false});
            var sketch = newSketch(context, id + "F26", { "sketchPlane" : qUnion([Q0])});
            skLineSegment(sketch, "E204.0", {"start": v(0.18, 618.48) * mm, "end": v(138.18, 582.92) * mm});
            skLineSegment(sketch, "E204.1", {"start": v(0.18, 618.48) * mm, "end": v(0.18, 283.37) * mm});
            skLineSegment(sketch, "E204.2", {"start": v(138.18, 582.92) * mm, "end": v(55.54, 269.6) * mm});
            skLineSegment(sketch, "E204.3", {"start": v(54.84, 266.97) * mm, "end": v(-0.31, 281.51) * mm});
            skLineSegment(sketch, "E205", {"start": v(0.18, 283.37) * mm, "end": v(0.18, 281.38) * mm});
            skLineSegment(sketch, "E206", {"start": v(55.54, 269.6) * mm, "end": v(54.84, 266.97) * mm});
            skSolve(sketch);
        }
    });
